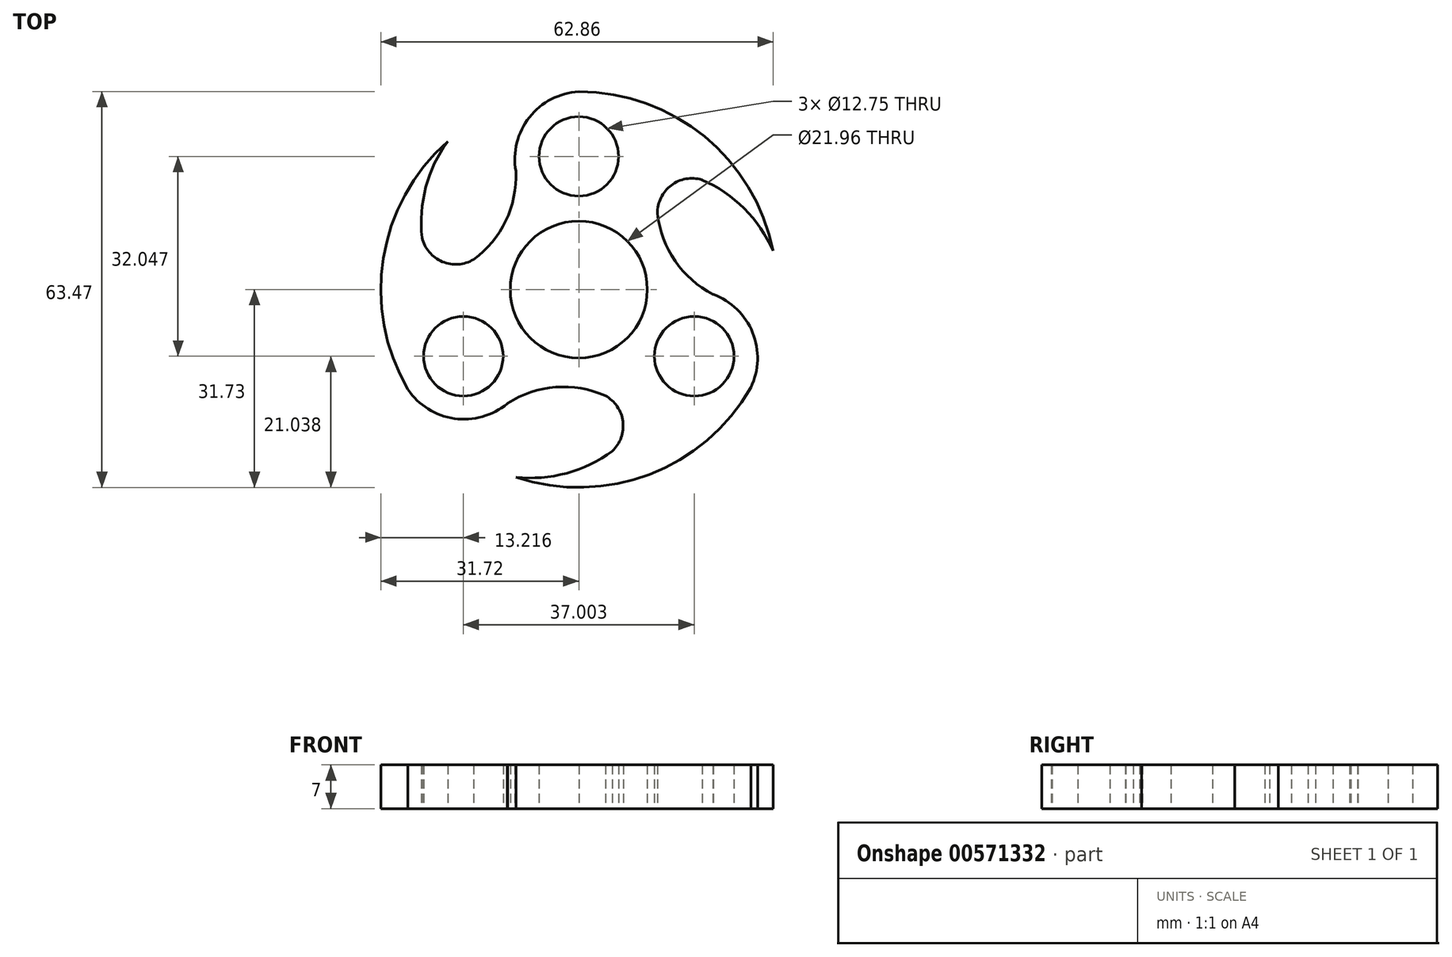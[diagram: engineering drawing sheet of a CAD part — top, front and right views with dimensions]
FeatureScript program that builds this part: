
annotation { "Feature Type Name" : "Feature", "Feature Type Description" : "" }
export const myFeature = defineFeature(function(context is Context, id is Id, definition is map)
    precondition{}
    {
        {
            var Q0;
            Q0=qCreatedBy(makeId("Top.planeOp"),FACE);
            var sketch = newSketch(context, id + "F0", { "sketchPlane" : qUnion([Q0])});
            skCircle(sketch, "E0", {"center": v(0, 0) * mm, "radius": 10.98 * mm});
            skCircle(sketch, "E1", {"center": v(0, 21.35) * mm, "radius": 6.38 * mm});
            skCircle(sketch, "E2.1.0", {"center": v(-18.5, -10.69) * mm, "radius": 6.38 * mm});
            skCircle(sketch, "E2.2.0", {"center": v(18.5, -10.7) * mm, "radius": 6.38 * mm});
            skArc(sketch, "E3.1.0", {"start": v(-0.03, 10.98) * mm, "mid": v(0.02, 10.98) * mm, "end": v(0.06, 10.98) * mm});
            skPoint(sketch, "E3.center", {"position": v(0.01, 0) * mm});
            skLineSegment(sketch, "E4.2.0", {"start": v(-21.47, -0.73) * mm, "end": v(-21.47, -0.73) * mm});
            skArc(sketch, "E5.trimOffspring", {"start": v(-9.33, -5.8) * mm, "mid": v(-9.5, -5.48) * mm, "end": v(-9.69, -5.17) * mm});
            skArc(sketch, "E6", {"start": v(10.11, 18.98) * mm, "mid": v(10.1, 18.97) * mm, "end": v(10.1, 18.96) * mm});
            skArc(sketch, "E7.1.3", {"start": v(-21.49, -0.73) * mm, "mid": v(-21.48, -0.73) * mm, "end": v(-21.47, -0.73) * mm});
            skArc(sketch, "E7.2.3", {"start": v(11.38, -18.25) * mm, "mid": v(11.38, -18.24) * mm, "end": v(11.37, -18.23) * mm});
            skLineSegment(sketch, "E8", {"start": v(-11.4, -18.23) * mm, "end": v(-11.45, -18.27) * mm});
            skPoint(sketch, "E9.orphan", {"position": v(-10.08, 18.99) * mm});
            skPoint(sketch, "E10.orphan", {"position": v(18.92, 15.55) * mm});
            skArc(sketch, "E11", {"start": v(31.14, 6.21) * mm, "mid": v(20.13, 24.55) * mm, "end": v(0, 31.74) * mm});
            skPoint(sketch, "E12.orphan", {"position": v(-29.05, -12.25) * mm});
            skPoint(sketch, "E13.orphan", {"position": v(3.91, 31.28) * mm});
            skPoint(sketch, "E14.orphan", {"position": v(25.14, -19.03) * mm});
            skArc(sketch, "E15", {"start": v(31.14, 6.21) * mm, "mid": v(26.52, 12.99) * mm, "end": v(19.75, 17.6) * mm});
            skArc(sketch, "E16", {"start": v(12.6, 12.2) * mm, "mid": v(15.43, 4.59) * mm, "end": v(21.52, -0.77) * mm});
            skArc(sketch, "E17.1.0", {"start": v(-20.95, 23.86) * mm, "mid": v(-24.5, 16.47) * mm, "end": v(-25.12, 8.3) * mm});
            skArc(sketch, "E17.1.1", {"start": v(-10.08, -30.08) * mm, "mid": v(11.32, -29.64) * mm, "end": v(27.57, -15.7) * mm});
            skArc(sketch, "E17.1.2", {"start": v(-16.86, 4.82) * mm, "mid": v(-11.71, 11.03) * mm, "end": v(-10.09, 18.92) * mm});
            skArc(sketch, "E17.2.0", {"start": v(-10.19, -30.07) * mm, "mid": v(-2.01, -29.46) * mm, "end": v(5.37, -25.9) * mm});
            skArc(sketch, "E17.2.2", {"start": v(4.26, -17.01) * mm, "mid": v(-3.73, -15.66) * mm, "end": v(-11.4, -18.23) * mm});
            skArc(sketch, "E18", {"start": v(0, 31.74) * mm, "mid": v(-7.91, 27.63) * mm, "end": v(-10.08, 18.99) * mm});
            skArc(sketch, "E19.1.0", {"start": v(-27.49, -15.87) * mm, "mid": v(-20.03, -20.66) * mm, "end": v(-11.49, -18.3) * mm});
            skArc(sketch, "E19.2.0", {"start": v(27.49, -15.87) * mm, "mid": v(27.9, -7) * mm, "end": v(21.54, -0.78) * mm});
            skArc(sketch, "E20", {"start": v(19.75, 17.6) * mm, "mid": v(14.8, 16.7) * mm, "end": v(12.6, 12.2) * mm});
            skPoint(sketch, "E21.orphan", {"position": v(13.38, 19.31) * mm});
            skArc(sketch, "E22.1.0", {"start": v(-25.12, 8.3) * mm, "mid": v(-21.87, 4.47) * mm, "end": v(-16.86, 4.82) * mm});
            skArc(sketch, "E22.2.0", {"start": v(5.37, -25.9) * mm, "mid": v(7.07, -21.18) * mm, "end": v(4.26, -17.01) * mm});
            skPoint(sketch, "E23.orphan", {"position": v(-23.42, 1.93) * mm});
            skPoint(sketch, "E24.orphan", {"position": v(10.04, -21.24) * mm});
            skArc(sketch, "E25.trimOffspring", {"start": v(-21.01, 23.77) * mm, "mid": v(-31.33, 5.01) * mm, "end": v(-27.38, -16.03) * mm});
            skArc(sketch, "E26.trimOffspring", {"start": v(-31.75, 0.02) * mm, "mid": v(-30.66, -8.2) * mm, "end": v(-27.49, -15.87) * mm});
            skLineSegment(sketch, "E27", {"start": v(-10.08, 18.99) * mm, "end": v(-10.09, 18.92) * mm});
            skLineSegment(sketch, "E28", {"start": v(-11.45, -18.27) * mm, "end": v(-11.49, -18.3) * mm});
            skPoint(sketch, "E29.orphan", {"position": v(-11.4, -18.23) * mm});
            skLineSegment(sketch, "E30", {"start": v(21.52, -0.77) * mm, "end": v(21.54, -0.78) * mm});
            skPoint(sketch, "E31.orphan", {"position": v(21.49, -0.76) * mm});
            skSolve(sketch);
        }
        {
            var Q0;
            Q0=qSketchRegion(id+"F0",true);
            extrude(context, id + "F1", {"entities" : qUnion([Q0]), "depth" : 7 * mm, "offsetDistance" : 25 * mm});
        }
    });
